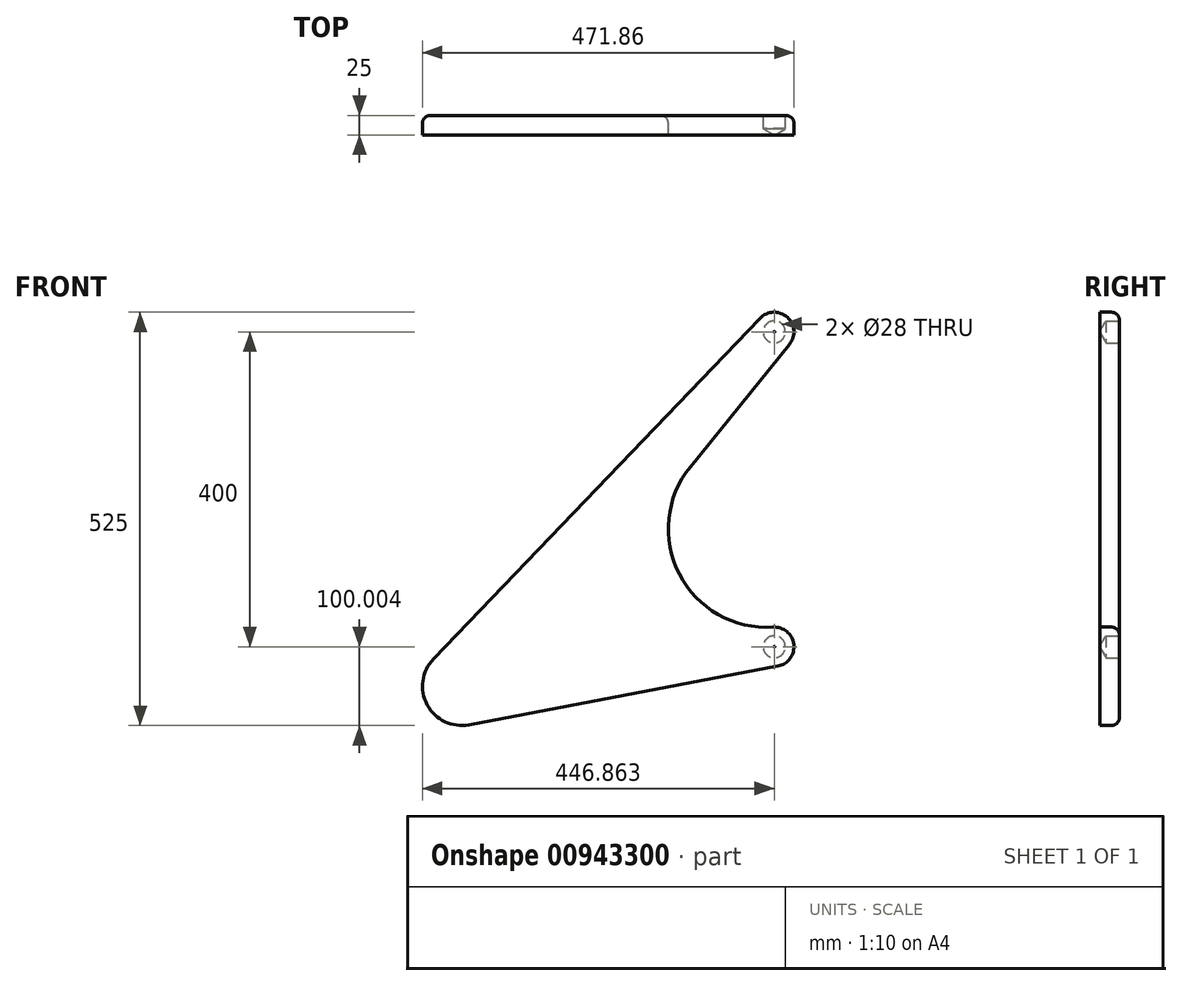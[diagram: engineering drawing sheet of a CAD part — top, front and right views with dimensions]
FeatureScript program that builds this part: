
annotation { "Feature Type Name" : "Feature", "Feature Type Description" : "" }
export const myFeature = defineFeature(function(context is Context, id is Id, definition is map)
    precondition{}
    {
        {
            var Q0;
            Q0=qCreatedBy(makeId("Front.planeOp"),FACE);
            var sketch = newSketch(context, id + "F0", { "sketchPlane" : qUnion([Q0])});
            skLineSegment(sketch, "E0", {"start": v(70.88, 564.87) * mm, "end": v(-325.98, 114.87) * mm});
            skLineSegment(sketch, "E1", {"start": v(-325.98, 114.87) * mm, "end": v(70.88, 164.87) * mm});
            skLineSegment(sketch, "E2", {"start": v(70.88, 164.87) * mm, "end": v(70.88, 564.87) * mm});
            skCircle(sketch, "E3", {"center": v(-325.98, 114.87) * mm, "radius": 50 * mm});
            skCircle(sketch, "E4", {"center": v(-325.98, 114.87) * mm, "radius": 30 * mm});
            skCircle(sketch, "E5", {"center": v(70.88, 164.87) * mm, "radius": 13.75 * mm});
            skCircle(sketch, "E6", {"center": v(70.88, 564.87) * mm, "radius": 13.75 * mm});
            skCircle(sketch, "E7", {"center": v(70.88, 564.87) * mm, "radius": 25 * mm});
            skCircle(sketch, "E8", {"center": v(70.88, 164.87) * mm, "radius": 25 * mm});
            skLineSegment(sketch, "E9", {"start": v(-362.07, 149.48) * mm, "end": v(52.84, 582.18) * mm});
            skLineSegment(sketch, "E10", {"start": v(-316.64, 65.75) * mm, "end": v(75.55, 140.31) * mm});
            skLineSegment(sketch, "E11", {"start": v(-287.13, 83.4) * mm, "end": v(90.3, 549.13) * mm});
            skLineSegment(sketch, "E12", {"start": v(69.31, 189.82) * mm, "end": v(-329.12, 164.78) * mm});
            skArc(sketch, "E13", {"start": v(69.31, 189.82) * mm, "mid": v(172.7, 372.13) * mm, "end": v(-35.78, 393.55) * mm});
            skCircle(sketch, "E14", {"center": v(61.46, 314.74) * mm, "radius": 125.17 * mm});
            skSolve(sketch);
        }
        {
            var Q0;
            {var subQ0=sQuery(id+"F0.wireOp",EDGE,"E9");Q0=makeQuery(id+"F0.imprint","IMPRINT",FACE,{"disambiguationData":[TD([[makeQuery(id+"F0.imprint","IMPRINT",EDGE,{"derivedFrom":subQ0}),-1.0]])]});}
            var Q1;
            {var subQ4=sQuery(id+"F0.wireOp",EDGE,"E7");var subQ5=sQuery(id+"F0.wireOp",EDGE,"E0");var subQ6=makeQuery(id+"F0.imprint","INTERSECT",VERTEX,{"derivedFrom":[subQ5,subQ4]});Q1=makeQuery(id+"F0.imprint","IMPRINT",FACE,{"disambiguationData":[TD([[makeQuery(id+"F0.imprint","IMPRINT",EDGE,{"disambiguationData":[TD([[subQ6,-1.0]])],"derivedFrom":subQ5}),1.0]])]});}
            var Q2;
            {var subQ1=sQuery(id+"F0.wireOp",EDGE,"E0");var subQ7=sQuery(id+"F0.wireOp",EDGE,"E12");var subQ9=makeQuery(id+"F0.imprint","INTERSECT",VERTEX,{"derivedFrom":[subQ1,subQ7]});Q2=makeQuery(id+"F0.imprint","IMPRINT",FACE,{"disambiguationData":[TD([[makeQuery(id+"F0.imprint","IMPRINT",EDGE,{"disambiguationData":[TD([[subQ9,-1.0]])],"derivedFrom":subQ1}),1.0]])]});}
            var Q3;
            {var subQ0=sQuery(id+"F0.wireOp",EDGE,"E12");var subQ1=sQuery(id+"F0.wireOp",EDGE,"E11");var subQ2=makeQuery(id+"F0.imprint","INTERSECT",VERTEX,{"derivedFrom":[subQ1,subQ0]});Q3=makeQuery(id+"F0.imprint","IMPRINT",FACE,{"disambiguationData":[TD([[makeQuery(id+"F0.imprint","IMPRINT",EDGE,{"disambiguationData":[TD([[subQ2,-1.0]])],"derivedFrom":subQ1}),-1.0]])]});}
            var Q4;
            {var subQ2=sQuery(id+"F0.wireOp",EDGE,"E0");var subQ6=sQuery(id+"F0.wireOp",EDGE,"E6");var subQ8=makeQuery(id+"F0.imprint","INTERSECT",VERTEX,{"derivedFrom":[subQ2,subQ6]});Q4=makeQuery(id+"F0.imprint","IMPRINT",FACE,{"disambiguationData":[TD([[makeQuery(id+"F0.imprint","IMPRINT",EDGE,{"disambiguationData":[TD([[subQ8,-1.0]])],"derivedFrom":subQ2}),-1.0]])]});}
            var Q5;
            {var subQ0=sQuery(id+"F0.wireOp",EDGE,"E6");var subQ1=sQuery(id+"F0.wireOp",EDGE,"E0");var subQ2=makeQuery(id+"F0.imprint","INTERSECT",VERTEX,{"derivedFrom":[subQ1,subQ0]});Q5=makeQuery(id+"F0.imprint","IMPRINT",FACE,{"disambiguationData":[TD([[makeQuery(id+"F0.imprint","IMPRINT",EDGE,{"disambiguationData":[TD([[subQ2,-1.0]])],"derivedFrom":subQ1}),1.0]])]});}
            var Q6;
            {var subQ0=sQuery(id+"F0.wireOp",EDGE,"E2");var subQ1=sQuery(id+"F0.wireOp",EDGE,"E0");var subQ2=makeQuery(id+"F0.imprint","INTERSECT",VERTEX,{"derivedFrom":[subQ1,subQ0]});Q6=makeQuery(id+"F0.imprint","IMPRINT",FACE,{"disambiguationData":[TD([[makeQuery(id+"F0.imprint","IMPRINT",EDGE,{"disambiguationData":[TD([[subQ2,-1.0]])],"derivedFrom":subQ1}),1.0]])]});}
            var Q7;
            {var subQ0=sQuery(id+"F0.wireOp",EDGE,"E2");var subQ1=sQuery(id+"F0.wireOp",EDGE,"E0");var subQ2=makeQuery(id+"F0.imprint","INTERSECT",VERTEX,{"derivedFrom":[subQ1,subQ0]});Q7=makeQuery(id+"F0.imprint","IMPRINT",FACE,{"disambiguationData":[TD([[makeQuery(id+"F0.imprint","IMPRINT",EDGE,{"disambiguationData":[TD([[subQ2,-1.0]])],"derivedFrom":subQ1}),-1.0]])]});}
            var Q8;
            {var subQ0=sQuery(id+"F0.wireOp",EDGE,"E11");var subQ1=sQuery(id+"F0.wireOp",EDGE,"E1");var subQ2=makeQuery(id+"F0.imprint","INTERSECT",VERTEX,{"derivedFrom":[subQ1,subQ0]});Q8=makeQuery(id+"F0.imprint","IMPRINT",FACE,{"disambiguationData":[TD([[makeQuery(id+"F0.imprint","IMPRINT",EDGE,{"disambiguationData":[TD([[subQ2,-1.0]])],"derivedFrom":subQ1}),1.0]])]});}
            var Q9;
            {var subQ0=sQuery(id+"F0.wireOp",EDGE,"E1");var subQ1=sQuery(id+"F0.wireOp",EDGE,"E0");var subQ2=makeQuery(id+"F0.imprint","INTERSECT",VERTEX,{"derivedFrom":[subQ1,subQ0]});Q9=makeQuery(id+"F0.imprint","IMPRINT",FACE,{"disambiguationData":[TD([[makeQuery(id+"F0.imprint","IMPRINT",EDGE,{"disambiguationData":[TD([[subQ2,1.0]])],"derivedFrom":subQ1}),-1.0]])]});}
            var Q10;
            {var subQ0=sQuery(id+"F0.wireOp",EDGE,"E3");var subQ2=sQuery(id+"F0.wireOp",EDGE,"E0");var subQ3=makeQuery(id+"F0.imprint","INTERSECT",VERTEX,{"derivedFrom":[subQ2,subQ0]});Q10=makeQuery(id+"F0.imprint","IMPRINT",FACE,{"disambiguationData":[TD([[makeQuery(id+"F0.imprint","IMPRINT",EDGE,{"disambiguationData":[TD([[subQ3,-1.0]])],"derivedFrom":subQ2}),-1.0]])]});}
            var Q11;
            {var subQ0=sQuery(id+"F0.wireOp",EDGE,"E3");var subQ1=sQuery(id+"F0.wireOp",EDGE,"E0");var subQ2=makeQuery(id+"F0.imprint","INTERSECT",VERTEX,{"derivedFrom":[subQ1,subQ0]});Q11=makeQuery(id+"F0.imprint","IMPRINT",FACE,{"disambiguationData":[TD([[makeQuery(id+"F0.imprint","IMPRINT",EDGE,{"disambiguationData":[TD([[subQ2,-1.0]])],"derivedFrom":subQ1}),1.0]])]});}
            var Q12;
            {var subQ0=sQuery(id+"F0.wireOp",EDGE,"E12");var subQ1=sQuery(id+"F0.wireOp",EDGE,"E0");var subQ2=makeQuery(id+"F0.imprint","INTERSECT",VERTEX,{"derivedFrom":[subQ1,subQ0]});Q12=makeQuery(id+"F0.imprint","IMPRINT",FACE,{"disambiguationData":[TD([[makeQuery(id+"F0.imprint","IMPRINT",EDGE,{"disambiguationData":[TD([[subQ2,-1.0]])],"derivedFrom":subQ1}),-1.0]])]});}
            var Q13;
            {var subQ0=sQuery(id+"F0.wireOp",EDGE,"E3");var subQ1=sQuery(id+"F0.wireOp",EDGE,"E1");var subQ2=makeQuery(id+"F0.imprint","INTERSECT",VERTEX,{"derivedFrom":[subQ1,subQ0]});Q13=makeQuery(id+"F0.imprint","IMPRINT",FACE,{"disambiguationData":[TD([[makeQuery(id+"F0.imprint","IMPRINT",EDGE,{"disambiguationData":[TD([[subQ2,-1.0]])],"derivedFrom":subQ1}),-1.0]])]});}
            var Q14;
            {var subQ0=sQuery(id+"F0.wireOp",EDGE,"E10");Q14=makeQuery(id+"F0.imprint","IMPRINT",FACE,{"disambiguationData":[TD([[makeQuery(id+"F0.imprint","IMPRINT",EDGE,{"derivedFrom":subQ0}),1.0]])]});}
            var Q15;
            {var subQ0=sQuery(id+"F0.wireOp",EDGE,"E1");var subQ1=sQuery(id+"F0.wireOp",EDGE,"E0");var subQ2=makeQuery(id+"F0.imprint","INTERSECT",VERTEX,{"derivedFrom":[subQ1,subQ0]});Q15=makeQuery(id+"F0.imprint","IMPRINT",FACE,{"disambiguationData":[TD([[makeQuery(id+"F0.imprint","IMPRINT",EDGE,{"disambiguationData":[TD([[subQ2,1.0]])],"derivedFrom":subQ1}),1.0]])]});}
            var Q16;
            {var subQ0=sQuery(id+"F0.wireOp",EDGE,"E8");var subQ5=sQuery(id+"F0.wireOp",EDGE,"E1");var subQ8=makeQuery(id+"F0.imprint","INTERSECT",VERTEX,{"derivedFrom":[subQ5,subQ0]});Q16=makeQuery(id+"F0.imprint","IMPRINT",FACE,{"disambiguationData":[TD([[makeQuery(id+"F0.imprint","IMPRINT",EDGE,{"disambiguationData":[TD([[subQ8,-1.0]])],"derivedFrom":subQ5}),1.0]])]});}
            var Q17;
            {var subQ0=sQuery(id+"F0.wireOp",EDGE,"E2");var subQ1=sQuery(id+"F0.wireOp",EDGE,"E1");var subQ2=makeQuery(id+"F0.imprint","INTERSECT",VERTEX,{"derivedFrom":[subQ1,subQ0]});Q17=makeQuery(id+"F0.imprint","IMPRINT",FACE,{"disambiguationData":[TD([[makeQuery(id+"F0.imprint","IMPRINT",EDGE,{"disambiguationData":[TD([[subQ2,1.0]])],"derivedFrom":subQ1}),1.0]])]});}
            var Q18;
            {var subQ0=sQuery(id+"F0.wireOp",EDGE,"E2");var subQ1=sQuery(id+"F0.wireOp",EDGE,"E1");var subQ2=makeQuery(id+"F0.imprint","INTERSECT",VERTEX,{"derivedFrom":[subQ1,subQ0]});Q18=makeQuery(id+"F0.imprint","IMPRINT",FACE,{"disambiguationData":[TD([[makeQuery(id+"F0.imprint","IMPRINT",EDGE,{"disambiguationData":[TD([[subQ2,1.0]])],"derivedFrom":subQ1}),-1.0]])]});}
            var Q19;
            {var subQ1=sQuery(id+"F0.wireOp",EDGE,"E1");var subQ5=sQuery(id+"F0.wireOp",EDGE,"E8");var subQ7=makeQuery(id+"F0.imprint","INTERSECT",VERTEX,{"derivedFrom":[subQ1,subQ5]});Q19=makeQuery(id+"F0.imprint","IMPRINT",FACE,{"disambiguationData":[TD([[makeQuery(id+"F0.imprint","IMPRINT",EDGE,{"disambiguationData":[TD([[subQ7,-1.0]])],"derivedFrom":subQ1}),-1.0]])]});}
            var Q20;
            {var subQ0=sQuery(id+"F0.wireOp",EDGE,"E11");var subQ1=sQuery(id+"F0.wireOp",EDGE,"E2");var subQ2=makeQuery(id+"F0.imprint","INTERSECT",VERTEX,{"derivedFrom":[subQ1,subQ0]});Q20=makeQuery(id+"F0.imprint","IMPRINT",FACE,{"disambiguationData":[TD([[makeQuery(id+"F0.imprint","IMPRINT",EDGE,{"disambiguationData":[TD([[subQ2,-1.0]])],"derivedFrom":subQ1}),-1.0]])]});}
            extrude(context, id + "F1", {"entities" : qUnion([Q0, Q1, Q2, Q3, Q4, Q5, Q6, Q7, Q8, Q9, Q10, Q11, Q12, Q13, Q14, Q15, Q16, Q17, Q18, Q19, Q20]), "depth" : 25 * mm, "offsetDistance" : 25 * mm});
        }
        {
            var Q0;
            Q0=sQuery(id+"F0.wireOp",VERTEX,"E0.start");
            var Q1;
            Q1=makeQuery(id+"F1.opExtrude","SWEPT_BODY",BODY,{"disambiguationData":[OSD([sQuery(id+"F0.wireOp",EDGE,"E3"),sQuery(id+"F0.wireOp",EDGE,"E7"),sQuery(id+"F0.wireOp",EDGE,"E8"),sQuery(id+"F0.wireOp",EDGE,"E9"),sQuery(id+"F0.wireOp",EDGE,"E10"),sQuery(id+"F0.wireOp",EDGE,"E11"),sQuery(id+"F0.wireOp",EDGE,"E14")])]});
            hole(context, id + "F2", {"style" : HoleStyle.SIMPLE, "endStyle" : HoleEndStyle.BLIND, "oppositeDirection" : true, "holeDiameter" : 28 * mm, "majorDiameter" : 5 * mm, "holeDepth" : 17 * mm, "isTappedThrough" : true, "tappedDepth" : 12 * mm, "tapClearance" : 3, "locations" : qUnion([Q0]), "scope" : qUnion([Q1])});
        }
        {
            var Q0;
            Q0=sQuery(id+"F0.wireOp",VERTEX,"E1.end");
            var Q1;
            Q1=makeQuery(id+"F1.opExtrude","SWEPT_BODY",BODY,{"disambiguationData":[OSD([sQuery(id+"F0.wireOp",EDGE,"E3"),sQuery(id+"F0.wireOp",EDGE,"E7"),sQuery(id+"F0.wireOp",EDGE,"E8"),sQuery(id+"F0.wireOp",EDGE,"E9"),sQuery(id+"F0.wireOp",EDGE,"E10"),sQuery(id+"F0.wireOp",EDGE,"E11"),sQuery(id+"F0.wireOp",EDGE,"E14")])]});
            hole(context, id + "F3", {"style" : HoleStyle.SIMPLE, "endStyle" : HoleEndStyle.BLIND, "oppositeDirection" : true, "holeDiameter" : 28 * mm, "majorDiameter" : 5 * mm, "holeDepth" : 17 * mm, "isTappedThrough" : true, "tappedDepth" : 12 * mm, "tapClearance" : 3, "locations" : qUnion([Q0]), "scope" : qUnion([Q1])});
        }
        {
            var Q0;
            Q0=makeQuery(id+"F1.opExtrude","CAP_EDGE",EDGE,{"disambiguationData":[OSD([sQuery(id+"F0.wireOp",EDGE,"E14")])],"isStart":true});
            var Q1;
            Q1=makeQuery(id+"F1.opExtrude","CAP_EDGE",EDGE,{"disambiguationData":[OSD([sQuery(id+"F0.wireOp",EDGE,"E8")])],"isStart":true});
            fillet(context, id + "F4", {"entities" : qUnion([Q0, Q1]), "radius" : 10 * mm, "tangentPropagation" : true, "allowEdgeOverflow" : false});
        }
        {
            var Q0;
            {var subQ0=sQuery(id+"F0.wireOp",EDGE,"E1");var subQ1=sQuery(id+"F0.wireOp",EDGE,"E0");var subQ2=makeQuery(id+"F0.imprint","INTERSECT",VERTEX,{"derivedFrom":[subQ1,subQ0]});Q0=makeQuery(id+"F0.imprint","IMPRINT",FACE,{"disambiguationData":[TD([[makeQuery(id+"F0.imprint","IMPRINT",EDGE,{"disambiguationData":[TD([[subQ2,1.0]])],"derivedFrom":subQ1}),-1.0]])]});}
            var Q1;
            {var subQ0=sQuery(id+"F0.wireOp",EDGE,"E1");var subQ1=sQuery(id+"F0.wireOp",EDGE,"E0");var subQ2=makeQuery(id+"F0.imprint","INTERSECT",VERTEX,{"derivedFrom":[subQ1,subQ0]});Q1=makeQuery(id+"F0.imprint","IMPRINT",FACE,{"disambiguationData":[TD([[makeQuery(id+"F0.imprint","IMPRINT",EDGE,{"disambiguationData":[TD([[subQ2,1.0]])],"derivedFrom":subQ1}),1.0]])]});}
            extrude(context, id + "F5", {"entities" : qUnion([Q0, Q1]), "operationType" : NewBodyOperationType.ADD, "depth" : 25 * mm, "offsetDistance" : 25 * mm});
        }
    });
